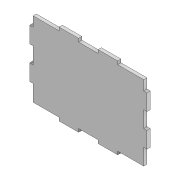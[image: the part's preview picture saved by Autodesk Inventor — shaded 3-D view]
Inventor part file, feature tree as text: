
AUTODESK INVENTOR PART (.ipt)
format: ipt  version: 2022 (Build 260153000, 153)  size: 122,368 bytes
history: native  units: mm
features: extrude x1, sketch x1
ambient origin geometry x8: Origin, YZ Plane, XZ Plane, XY Plane, X Axis, Y Axis, Z Axis, Center Point
bodies: Solid1 (feature_tree)
feature tree (2):
  extrude  "Extrusion1"  Depth=115.0mm
  sketch  "Sketch1"  dims[d0=170.0mm d1=115.0mm d2=30.0mm d3=5.0mm d4=30.0mm d5=5.0mm d6=30.0mm d7=40.0mm d8=5.0mm d9=25.0mm d10=5.0mm d11=25.0mm d12=25.0mm d13=15.0mm d14=5.0mm d15=0.0mm]
